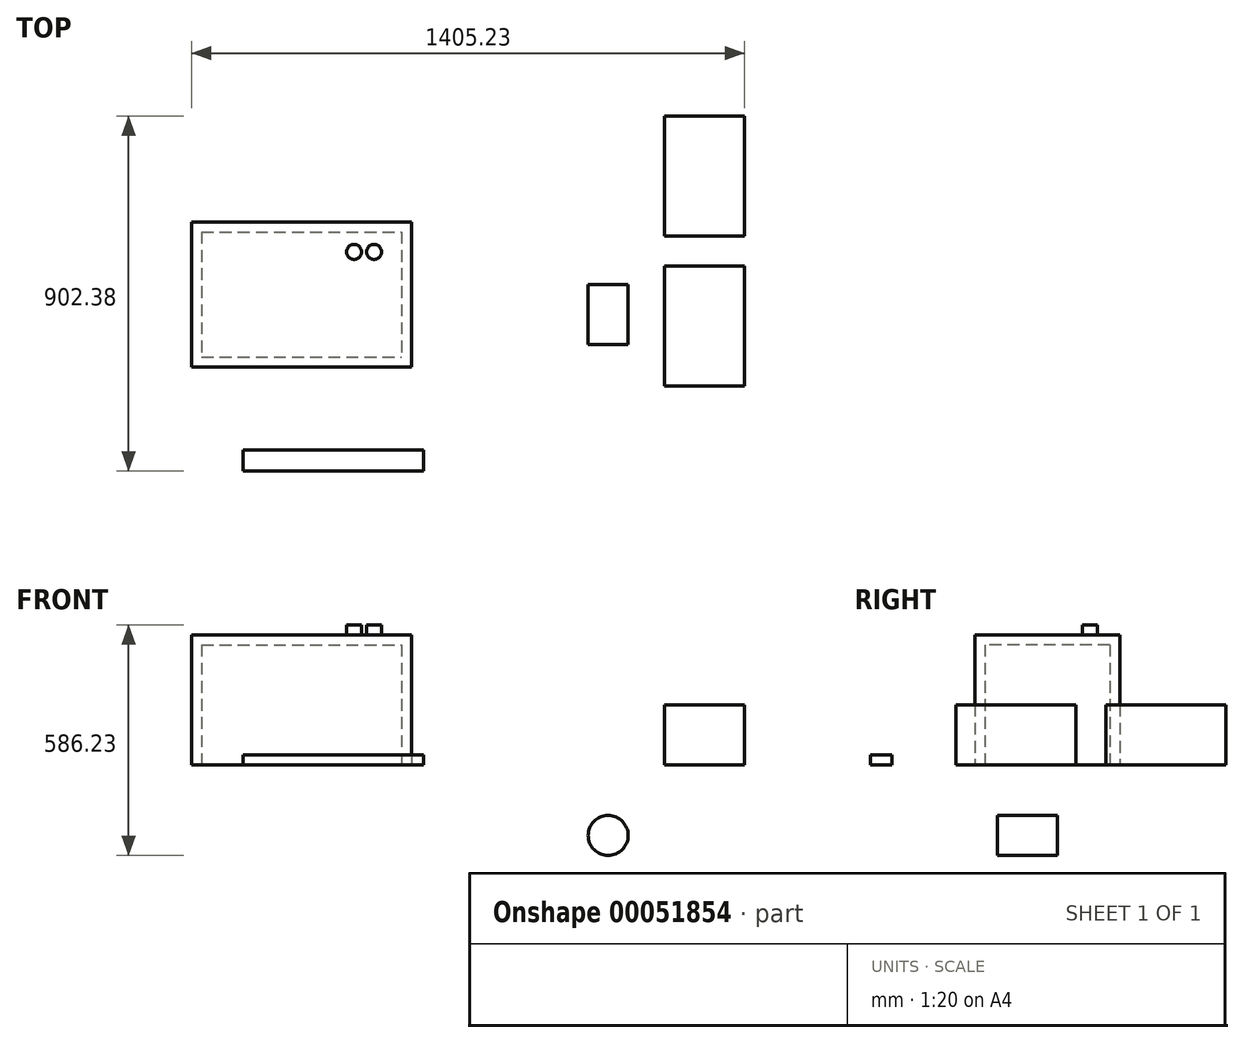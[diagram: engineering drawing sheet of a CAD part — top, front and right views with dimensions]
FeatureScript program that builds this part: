
annotation { "Feature Type Name" : "Feature", "Feature Type Description" : "" }
export const myFeature = defineFeature(function(context is Context, id is Id, definition is map)
    precondition{}
    {
        {
            var Q0;
            Q0=qCreatedBy(makeId("Top.planeOp"),FACE);
            var sketch = newSketch(context, id + "F0", { "sketchPlane" : qUnion([Q0])});
            skLineSegment(sketch, "E0.bottom", {"start": v(-258.47, 159.12) * mm, "end": v(300.33, 159.12) * mm});
            skLineSegment(sketch, "E0.top", {"start": v(-258.47, -209.18) * mm, "end": v(300.33, -209.18) * mm});
            skLineSegment(sketch, "E0.left", {"start": v(-258.47, 159.12) * mm, "end": v(-258.47, -209.18) * mm});
            skLineSegment(sketch, "E0.right", {"start": v(300.33, 159.12) * mm, "end": v(300.33, -209.18) * mm});
            skLineSegment(sketch, "E1.bottom", {"start": v(-233.07, 133.72) * mm, "end": v(274.93, 133.72) * mm});
            skLineSegment(sketch, "E1.right", {"start": v(274.93, 133.72) * mm, "end": v(274.93, -183.78) * mm});
            skLineSegment(sketch, "E2.bottom", {"start": v(-233.07, -183.78) * mm, "end": v(274.93, -183.78) * mm});
            skLineSegment(sketch, "E3.right", {"start": v(-233.07, 133.72) * mm, "end": v(-233.07, -183.78) * mm});
            skSolve(sketch);
        }
        {
            var Q0;
            Q0=makeQuery(id+"F0.imprint","IMPRINT",FACE,{"disambiguationData":[TD([[makeQuery(id+"F0.imprint","IMPRINT",EDGE,{"derivedFrom":sQuery(id+"F0.wireOp",EDGE,"E0.bottom")}),-1.0]])]});
            extrude(context, id + "F1", {"entities" : qUnion([Q0]), "depth" : 304.8 * mm});
        }
        {
            var Q0;
            Q0=makeQuery(id+"F1.opExtrude","CAP_FACE",FACE,{"disambiguationData":[OSD([sQuery(id+"F0.wireOp",EDGE,"E0.bottom"),sQuery(id+"F0.wireOp",EDGE,"E0.top"),sQuery(id+"F0.wireOp",EDGE,"E0.left"),sQuery(id+"F0.wireOp",EDGE,"E0.right")])],"isStart":false});
            var sketch = newSketch(context, id + "F2", { "sketchPlane" : qUnion([Q0])});
            skCircle(sketch, "E4", {"center": v(205.12, 82.92) * mm, "radius": 19.05 * mm});
            skCircle(sketch, "E5", {"center": v(154.32, 82.92) * mm, "radius": 19.05 * mm});
            skLineSegment(sketch, "E6.bottom", {"start": v(-258.47, 159.12) * mm, "end": v(300.33, 159.12) * mm});
            skLineSegment(sketch, "E6.top", {"start": v(-258.47, -209.18) * mm, "end": v(300.33, -209.18) * mm});
            skLineSegment(sketch, "E6.left", {"start": v(-258.47, 159.12) * mm, "end": v(-258.47, -209.18) * mm});
            skLineSegment(sketch, "E6.right", {"start": v(300.33, 159.12) * mm, "end": v(300.33, -209.18) * mm});
            skSolve(sketch);
        }
        {
            var Q0;
            Q0=makeQuery(id+"F2.imprint","IMPRINT",FACE,{"disambiguationData":[TD([[makeQuery(id+"F2.imprint","IMPRINT",EDGE,{"derivedFrom":sQuery(id+"F2.wireOp",EDGE,"E6.bottom")}),-1.0]])]});
            var Q1;
            Q1=makeQuery(id+"F2.imprint","IMPRINT",FACE,{"disambiguationData":[TD([[makeQuery(id+"F2.imprint","IMPRINT",EDGE,{"derivedFrom":sQuery(id+"F2.wireOp",EDGE,"E4")}),-1.0]])]});
            extrude(context, id + "F3", {"entities" : qUnion([Q0, Q1]), "operationType" : NewBodyOperationType.ADD, "depth" : 25.4 * mm});
        }
        {
            var Q0;
            Q0=makeQuery(id+"F2.imprint","IMPRINT",FACE,{"disambiguationData":[TD([[makeQuery(id+"F2.imprint","IMPRINT",EDGE,{"derivedFrom":sQuery(id+"F2.wireOp",EDGE,"E5")}),1.0]])]});
            var Q1;
            Q1=makeQuery(id+"F2.imprint","IMPRINT",FACE,{"disambiguationData":[TD([[makeQuery(id+"F2.imprint","IMPRINT",EDGE,{"derivedFrom":sQuery(id+"F2.wireOp",EDGE,"E4")}),1.0]])]});
            extrude(context, id + "F4", {"entities" : qUnion([Q0, Q1]), "operationType" : NewBodyOperationType.ADD, "depth" : 50.8 * mm});
        }
        {
            var Q0;
            Q0=qCreatedBy(makeId("Front.planeOp"),FACE);
            var sketch = newSketch(context, id + "F5", { "sketchPlane" : qUnion([Q0])});
            skCircle(sketch, "E7", {"center": v(799.88, -179.83) * mm, "radius": 50.8 * mm});
            skSolve(sketch);
        }
        {
            var Q0;
            Q0=makeQuery(id+"F5.imprint","IMPRINT",FACE,{"disambiguationData":[TD([[makeQuery(id+"F5.imprint","IMPRINT",EDGE,{"derivedFrom":sQuery(id+"F5.wireOp",EDGE,"E7")}),1.0]])]});
            extrude(context, id + "F6", {"entities" : qUnion([Q0]), "depth" : 152.4 * mm});
        }
        {
            var Q0;
            Q0=qCreatedBy(makeId("Top.planeOp"),FACE);
            var sketch = newSketch(context, id + "F7", { "sketchPlane" : qUnion([Q0])});
            skLineSegment(sketch, "E8.bottom", {"start": v(330.6, -420.15) * mm, "end": v(-128.13, -420.15) * mm});
            skLineSegment(sketch, "E8.top", {"start": v(330.6, -474.22) * mm, "end": v(-128.13, -474.22) * mm});
            skLineSegment(sketch, "E8.left", {"start": v(330.6, -420.15) * mm, "end": v(330.6, -474.22) * mm});
            skLineSegment(sketch, "E8.right", {"start": v(-128.13, -420.15) * mm, "end": v(-128.13, -474.22) * mm});
            skSolve(sketch);
        }
        {
            var Q0;
            Q0=makeQuery(id+"F7.imprint","IMPRINT",FACE,{"disambiguationData":[TD([[makeQuery(id+"F7.imprint","IMPRINT",EDGE,{"derivedFrom":sQuery(id+"F7.wireOp",EDGE,"E8.bottom")}),1.0]])]});
            extrude(context, id + "F8", {"entities" : qUnion([Q0]), "depth" : 25.4 * mm});
        }
        {
            var Q0;
            Q0=qCreatedBy(makeId("Top.planeOp"),FACE);
            var sketch = newSketch(context, id + "F9", { "sketchPlane" : qUnion([Q0])});
            skLineSegment(sketch, "E9.bottom", {"start": v(943.56, 47.16) * mm, "end": v(1146.76, 47.16) * mm});
            skLineSegment(sketch, "E9.top", {"start": v(943.56, -257.64) * mm, "end": v(1146.76, -257.64) * mm});
            skLineSegment(sketch, "E9.left", {"start": v(943.56, 47.16) * mm, "end": v(943.56, -257.64) * mm});
            skLineSegment(sketch, "E9.right", {"start": v(1146.76, 47.16) * mm, "end": v(1146.76, -257.64) * mm});
            skSolve(sketch);
        }
        {
            var Q0;
            Q0=makeQuery(id+"F9.imprint","IMPRINT",FACE,{"disambiguationData":[TD([[makeQuery(id+"F9.imprint","IMPRINT",EDGE,{"derivedFrom":sQuery(id+"F9.wireOp",EDGE,"E9.bottom")}),-1.0]])]});
            extrude(context, id + "F10", {"entities" : qUnion([Q0]), "depth" : 152.4 * mm});
        }
        {
            var Q0;
            Q0=makeQuery(id+"F10.opExtrude","SWEPT_BODY",BODY,{"disambiguationData":[OSD([sQuery(id+"F9.wireOp",EDGE,"E9.bottom"),sQuery(id+"F9.wireOp",EDGE,"E9.top"),sQuery(id+"F9.wireOp",EDGE,"E9.left"),sQuery(id+"F9.wireOp",EDGE,"E9.right")])]});
            transform(context, id + "F11", {"entities" : qUnion([Q0]), "transformType" : TransformType.TRANSLATION_3D, "dx" : 0 * mm, "dy" : 381 * mm, "dz" : 0 * mm, "makeCopy" : true});
        }
    });
